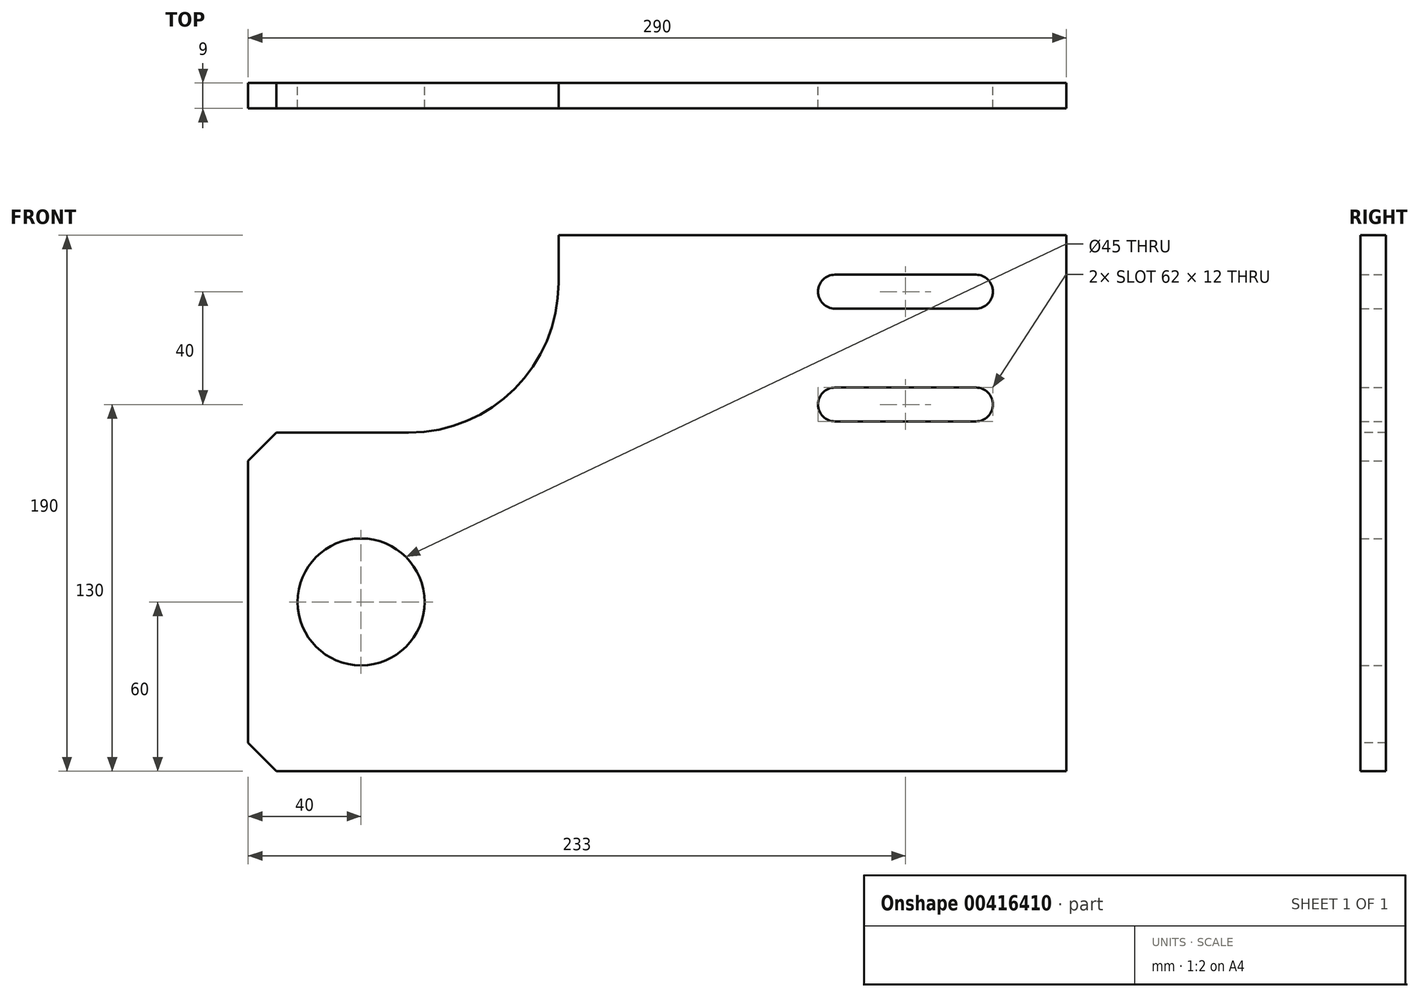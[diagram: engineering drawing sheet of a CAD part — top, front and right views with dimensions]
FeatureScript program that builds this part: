
annotation { "Feature Type Name" : "Feature", "Feature Type Description" : "" }
export const myFeature = defineFeature(function(context is Context, id is Id, definition is map)
    precondition{}
    {
        {
            var Q0;
            Q0=qCreatedBy(makeId("Front.planeOp"),FACE);
            var sketch = newSketch(context, id + "F0", { "sketchPlane" : qUnion([Q0])});
            skLineSegment(sketch, "E0", {"start": v(0, 0) * mm, "end": v(0, 190) * mm});
            skLineSegment(sketch, "E1", {"start": v(0, 190) * mm, "end": v(-180, 190) * mm});
            skLineSegment(sketch, "E2", {"start": v(-180, 190) * mm, "end": v(-180, 120) * mm});
            skLineSegment(sketch, "E3", {"start": v(-180, 120) * mm, "end": v(-290, 120) * mm});
            skLineSegment(sketch, "E4", {"start": v(-290, 120) * mm, "end": v(-290, 0) * mm});
            skLineSegment(sketch, "E5", {"start": v(-290, 0) * mm, "end": v(0, 0) * mm});
            skSolve(sketch);
        }
        {
            var Q0;
            Q0 = qSketchRegion(id + "F0", true);
            extrude(context, id + "F1", {"entities" : qUnion([Q0]), "depth" : 9 * mm});
        }
        {
            var Q0;
            Q0=qCreatedBy(makeId("Front.planeOp"),FACE);
            var sketch = newSketch(context, id + "F2", { "sketchPlane" : qUnion([Q0])});
            skLineSegment(sketch, "E6", {"start": v(-82, 176) * mm, "end": v(-32, 176) * mm});
            skLineSegment(sketch, "E7", {"start": v(-82, 164) * mm, "end": v(-32, 164) * mm});
            skArc(sketch, "E8", {"start": v(-82, 176) * mm, "mid": v(-88, 170) * mm, "end": v(-82, 164) * mm});
            skPoint(sketch, "E9.center.orphan", {"position": v(-32, 170) * mm});
            skArc(sketch, "E10", {"start": v(-32, 164) * mm, "mid": v(-26, 170) * mm, "end": v(-32, 176) * mm});
            skArc(sketch, "E11.0.1.0", {"start": v(-82, 136) * mm, "mid": v(-88, 130) * mm, "end": v(-82, 124) * mm});
            skLineSegment(sketch, "E11.0.1.1", {"start": v(-82, 124) * mm, "end": v(-32, 124) * mm});
            skLineSegment(sketch, "E11.0.1.2", {"start": v(-82, 136) * mm, "end": v(-32, 136) * mm});
            skPoint(sketch, "E11.0.1.3", {"position": v(-32, 130) * mm});
            skArc(sketch, "E11.0.1.4", {"start": v(-32, 124) * mm, "mid": v(-26, 130) * mm, "end": v(-32, 136) * mm});
            skArc(sketch, "E11.1.1.0", {"start": v(-82, 136) * mm, "mid": v(-88, 130) * mm, "end": v(-82, 124) * mm});
            skLineSegment(sketch, "E11.1.1.1", {"start": v(-82, 124) * mm, "end": v(-32, 124) * mm});
            skLineSegment(sketch, "E11.1.1.2", {"start": v(-82, 136) * mm, "end": v(-32, 136) * mm});
            skPoint(sketch, "E11.1.1.3", {"position": v(-32, 130) * mm});
            skArc(sketch, "E11.1.1.4", {"start": v(-32, 124) * mm, "mid": v(-26, 130) * mm, "end": v(-32, 136) * mm});
            skArc(sketch, "E11.2.1.0", {"start": v(-82, 136) * mm, "mid": v(-88, 130) * mm, "end": v(-82, 124) * mm});
            skLineSegment(sketch, "E11.2.1.1", {"start": v(-82, 124) * mm, "end": v(-32, 124) * mm});
            skLineSegment(sketch, "E11.2.1.2", {"start": v(-82, 136) * mm, "end": v(-32, 136) * mm});
            skPoint(sketch, "E11.2.1.3", {"position": v(-32, 130) * mm});
            skArc(sketch, "E11.2.1.4", {"start": v(-32, 124) * mm, "mid": v(-26, 130) * mm, "end": v(-32, 136) * mm});
            skLineSegment(sketch, "E11.direction1", {"start": v(-82, 164) * mm, "end": v(-82, 164) * mm});
            skLineSegment(sketch, "E11.direction2", {"start": v(-82, 164) * mm, "end": v(-82, 124) * mm, "construction": true});
            skCircle(sketch, "E12", {"center": v(-250, 60) * mm, "radius": 22.5 * mm});
            skSolve(sketch);
        }
        {
            var Q0;
            Q0 = qSketchRegion(id + "F2", true);
            extrude(context, id + "F3", {"entities" : qUnion([Q0]), "operationType" : NewBodyOperationType.REMOVE, "endBound" : BoundingType.THROUGH_ALL, "depth" : 25 * mm});
        }
        {
            var Q0;
            Q0=makeQuery(id+"F1.opExtrude","SWEPT_EDGE",EDGE,{"disambiguationData":[OSD([sQuery(id+"F0.wireOp",EDGE,"E2"),sQuery(id+"F0.wireOp",EDGE,"E3")])]});
            fillet(context, id + "F4", {"entities" : qUnion([Q0]), "radius" : 53.1 * mm, "tangentPropagation" : true, "allowEdgeOverflow" : false});
        }
        {
            var Q0;
            Q0=makeQuery(id+"F1.opExtrude","SWEPT_EDGE",EDGE,{"disambiguationData":[OSD([sQuery(id+"F0.wireOp",EDGE,"E4"),sQuery(id+"F0.wireOp",EDGE,"E5")])]});
            var Q1;
            Q1=makeQuery(id+"F1.opExtrude","SWEPT_EDGE",EDGE,{"disambiguationData":[OSD([sQuery(id+"F0.wireOp",EDGE,"E3"),sQuery(id+"F0.wireOp",EDGE,"E4")])]});
            chamfer(context, id + "F5", {"entities" : qUnion([Q0, Q1]), "width" : (10) * mm, "tangentPropagation" : true});
        }
        {
            var Q0;
            Q0=makeQuery(id+"F5.opChamfer","BLEND_FACE",FACE,{"disambiguationData":[OSD([sQuery(id+"F0.wireOp",EDGE,"E3"),sQuery(id+"F0.wireOp",EDGE,"E4")])]});
            cPlane(context, id + "F6", {"entities" : qUnion([Q0]), "cplaneType" : CPlaneType.OFFSET, "offset" : 0 * mm, "width" : 150 * mm, "height" : 150 * mm});
        }
        {
            var Q0;
            Q0=makeQuery(id+"F5.opChamfer","BLEND_FACE",FACE,{"disambiguationData":[OSD([sQuery(id+"F0.wireOp",EDGE,"E4"),sQuery(id+"F0.wireOp",EDGE,"E5")])]});
            var sketch = newSketch(context, id + "F7", { "sketchPlane" : qUnion([Q0])});
            skSolve(sketch);
        }
    });
